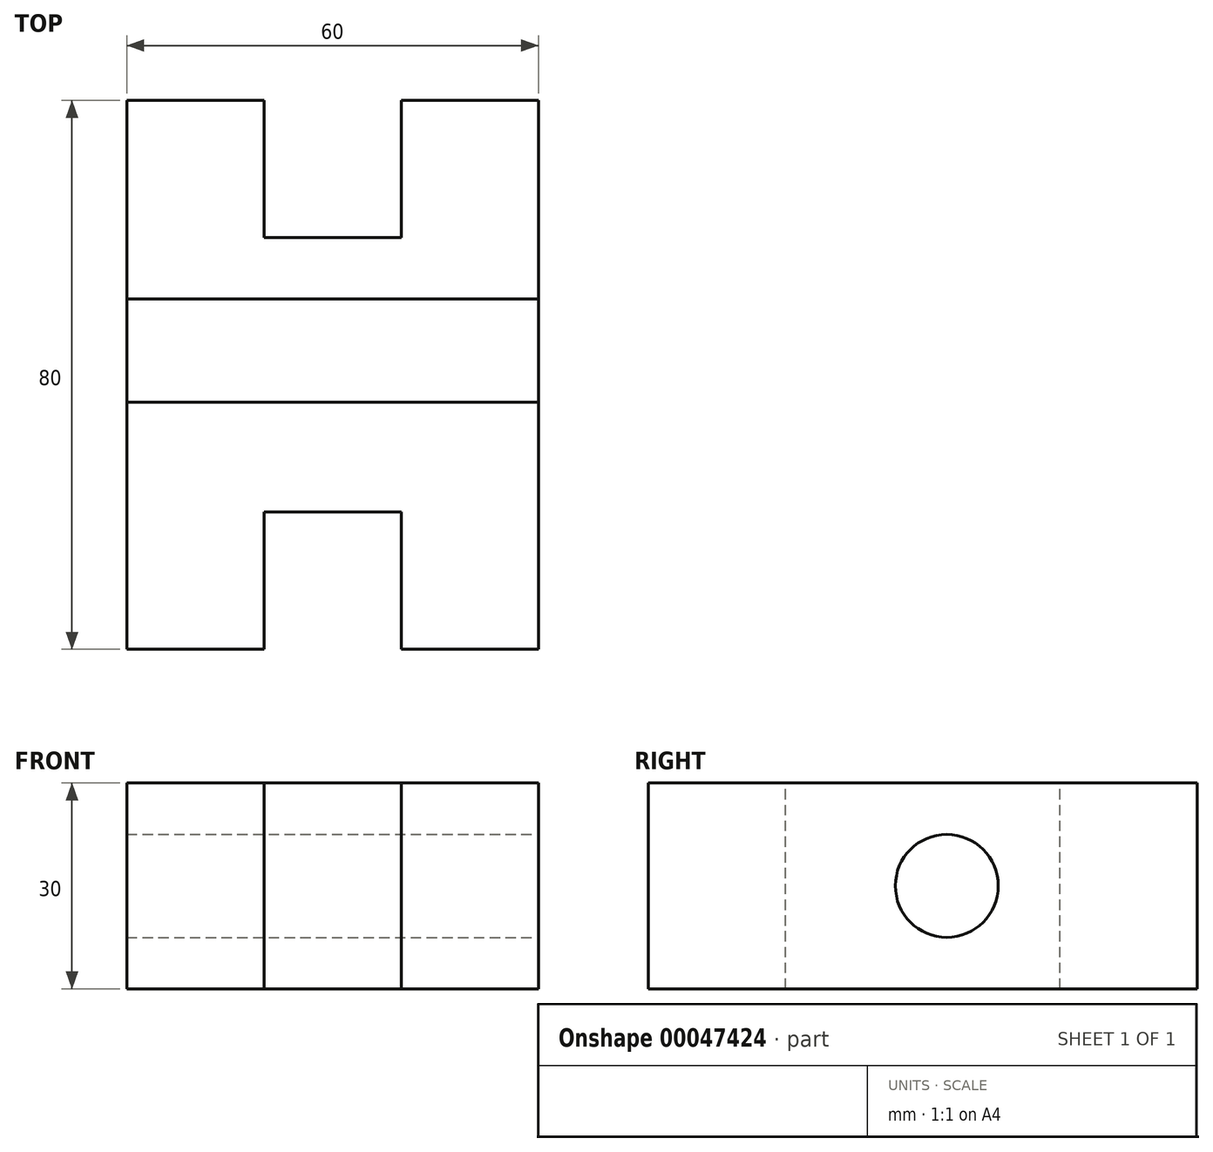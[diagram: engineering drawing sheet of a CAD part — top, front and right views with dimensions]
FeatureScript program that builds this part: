
annotation { "Feature Type Name" : "Feature", "Feature Type Description" : "" }
export const myFeature = defineFeature(function(context is Context, id is Id, definition is map)
    precondition{}
    {
        {
            var Q0;
            Q0=qCreatedBy(makeId("Top.planeOp"),FACE);
            var sketch = newSketch(context, id + "F0", { "sketchPlane" : qUnion([Q0])});
            skLineSegment(sketch, "E0", {"start": v(-40, 38.23) * mm, "end": v(-40, -41.77) * mm});
            skLineSegment(sketch, "E1", {"start": v(-40, -41.77) * mm, "end": v(-20, -41.77) * mm});
            skLineSegment(sketch, "E2", {"start": v(-40, 38.23) * mm, "end": v(-20, 38.23) * mm});
            skLineSegment(sketch, "E3", {"start": v(-20, 38.23) * mm, "end": v(-20, 18.23) * mm});
            skLineSegment(sketch, "E4", {"start": v(-20, -41.77) * mm, "end": v(-20, -21.77) * mm});
            skLineSegment(sketch, "E5", {"start": v(-20, 18.23) * mm, "end": v(0, 18.23) * mm});
            skLineSegment(sketch, "E6", {"start": v(-20, -21.77) * mm, "end": v(0, -21.77) * mm});
            skLineSegment(sketch, "E7", {"start": v(0, 18.23) * mm, "end": v(0, 38.23) * mm});
            skLineSegment(sketch, "E8", {"start": v(0, -21.77) * mm, "end": v(0, -41.77) * mm});
            skLineSegment(sketch, "E9", {"start": v(0, -41.77) * mm, "end": v(20, -41.77) * mm});
            skLineSegment(sketch, "E10", {"start": v(0, 38.23) * mm, "end": v(20, 38.23) * mm});
            skLineSegment(sketch, "E11", {"start": v(20, 38.23) * mm, "end": v(20, -41.77) * mm});
            skSolve(sketch);
        }
        {
            var Q0;
            Q0 = qSketchRegion(id + "F0", true);
            var Q1;
            Q1=sQuery(id+"F0.wireOp",EDGE,"E2");
            var Q2;
            Q2=sQuery(id+"F0.wireOp",EDGE,"E0");
            var Q3;
            Q3=sQuery(id+"F0.wireOp",EDGE,"E1");
            var Q4;
            Q4=sQuery(id+"F0.wireOp",EDGE,"E4");
            var Q5;
            Q5=sQuery(id+"F0.wireOp",EDGE,"E6");
            var Q6;
            Q6=sQuery(id+"F0.wireOp",EDGE,"E5");
            var Q7;
            Q7=sQuery(id+"F0.wireOp",EDGE,"E10");
            var Q8;
            Q8=sQuery(id+"F0.wireOp",EDGE,"E11");
            var Q9;
            Q9=sQuery(id+"F0.wireOp",EDGE,"E9");
            var Q10;
            Q10=sQuery(id+"F0.wireOp",EDGE,"E3");
            var Q11;
            Q11=sQuery(id+"F0.wireOp",EDGE,"E7");
            var Q12;
            Q12=sQuery(id+"F0.wireOp",EDGE,"E8");
            extrude(context, id + "F1", {"entities" : qUnion([Q0]), "bodyType" : ToolBodyType.SURFACE, "surfaceEntities" : qUnion([Q1, Q2, Q3, Q4, Q5, Q6, Q7, Q8, Q9, Q10, Q11, Q12]), "depth" : 30 * mm});
        }
        {
            var Q0;
            Q0=makeQuery(id+"F1.opExtrude","SWEPT_FACE",FACE,{"disambiguationData":[OSD([sQuery(id+"F0.wireOp",EDGE,"E0")])]});
            var sketch = newSketch(context, id + "F2", { "sketchPlane" : qUnion([Q0])});
            skCircle(sketch, "E12", {"center": v(1.77, 15) * mm, "radius": 7.5 * mm});
            skSolve(sketch);
        }
        {
            var Q0;
            Q0 = qSketchRegion(id + "F2", true);
            var Q1;
            Q1=sQuery(id+"F2.wireOp",EDGE,"E12");
            extrude(context, id + "F3", {"entities" : qUnion([Q0]), "bodyType" : ToolBodyType.SURFACE, "operationType" : NewBodyOperationType.REMOVE, "surfaceEntities" : qUnion([Q1]), "depth" : 60 * mm});
        }
    });
